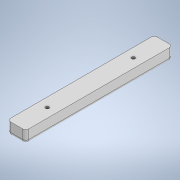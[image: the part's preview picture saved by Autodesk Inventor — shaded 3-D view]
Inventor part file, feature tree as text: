
AUTODESK INVENTOR PART (.ipt)
format: ipt  version: 2020 (Build 240168000, 168)  size: 120,320 bytes
history: native  units: in
note: dims shown in document units (in); Inventor stores cm internally (conversion verified against a paired STEP export)
features: extrude x2, sketch x2, fillet x1
ambient origin geometry x8: Origin, YZ Plane, XZ Plane, XY Plane, X Axis, Y Axis, Z Axis, Center Point
bodies: Solid1 (feature_tree)
feature tree (5):
  extrude  "Extrusion1"  Depth=0.75in
  extrude  "Extrusion2"  Depth=0.125in
  fillet  "Fillet1"  Radius=0.1406in
  sketch  "Sketch1"  dims[d0=6.0in d1=0.75in]
  sketch  "Sketch2"  dims[d2=0.5in d3=0.0in d4=0.1406in d5=0.1406in d6=1.375in d7=0.0in d8=0.125in]
